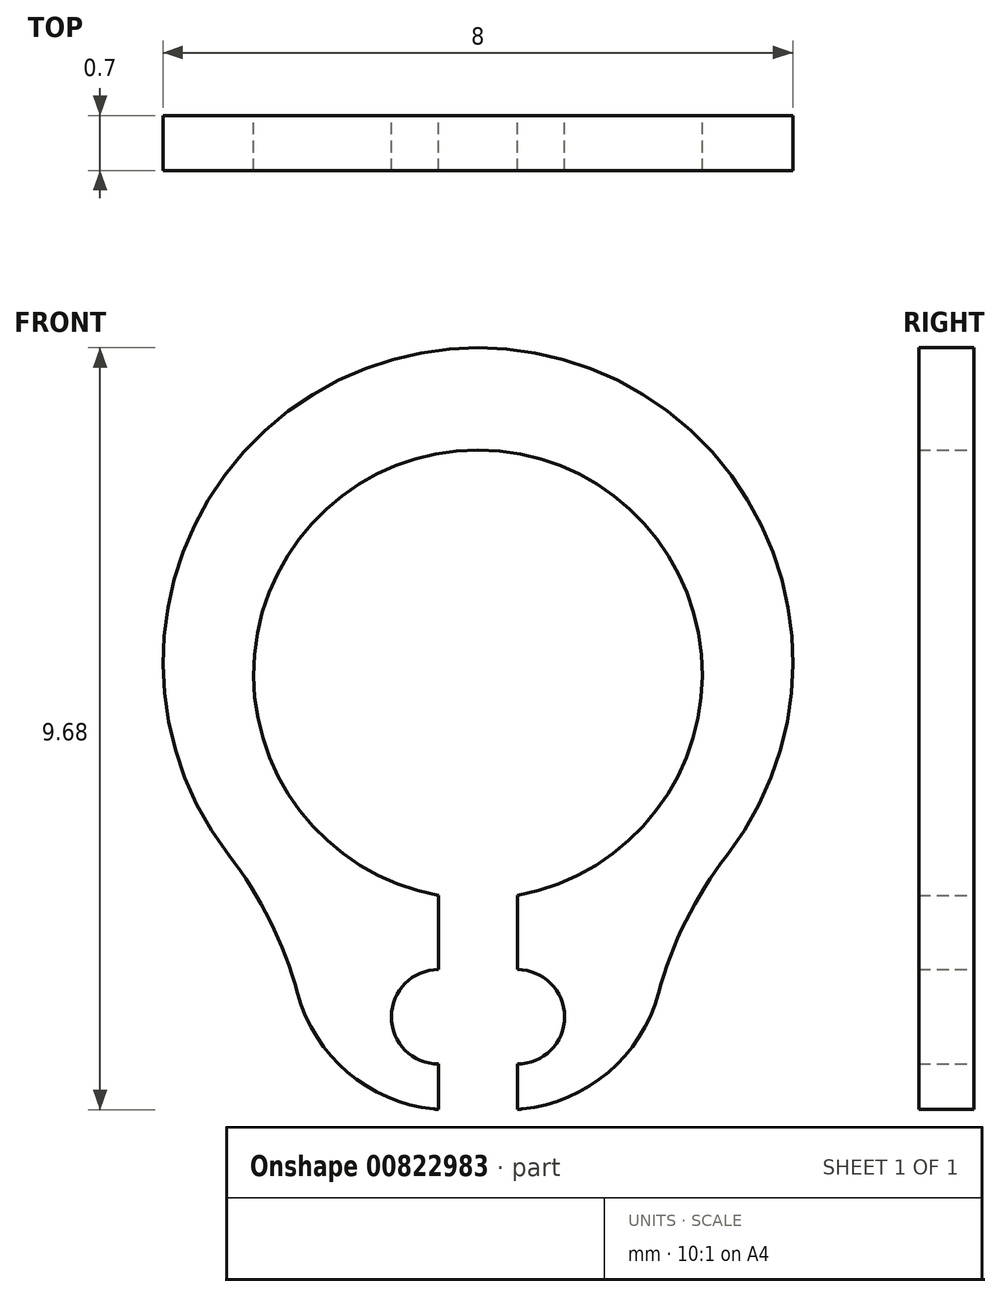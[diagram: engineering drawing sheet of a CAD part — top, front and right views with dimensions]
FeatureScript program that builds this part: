
annotation { "Feature Type Name" : "Feature", "Feature Type Description" : "" }
export const myFeature = defineFeature(function(context is Context, id is Id, definition is map)
    precondition{}
    {
        {
            var Q0;
            Q0=qCreatedBy(makeId("Front.planeOp"),FACE);
            var sketch = newSketch(context, id + "F0", { "sketchPlane" : qUnion([Q0])});
            skArc(sketch, "E0", {"start": v(0.5, -2.8) * mm, "mid": v(0, 2.85) * mm, "end": v(-0.5, -2.8) * mm});
            skLineSegment(sketch, "E1", {"start": v(0, 0) * mm, "end": v(0, -5.55) * mm, "construction": true});
            skLineSegment(sketch, "E2", {"start": v(0, 0) * mm, "end": v(0, 2.85) * mm, "construction": true});
            skLineSegment(sketch, "E3", {"start": v(0, 2.85) * mm, "end": v(0, 4.15) * mm, "construction": true});
            skPoint(sketch, "E4", {"position": v(0, -2.85) * mm});
            skArc(sketch, "E5", {"start": v(-2.12, -5.13) * mm, "mid": v(-1.33, -5.39) * mm, "end": v(-0.5, -5.53) * mm});
            skArc(sketch, "E6", {"start": v(1.48, -3.57) * mm, "mid": v(0, 4.15) * mm, "end": v(-1.48, -3.57) * mm});
            skPoint(sketch, "E7", {"position": v(0, -3.85) * mm});
            skArc(sketch, "E8", {"start": v(0.5, -4.95) * mm, "mid": v(1.1, -4.35) * mm, "end": v(0.5, -3.75) * mm});
            skLineSegment(sketch, "E9", {"start": v(0, 0) * mm, "end": v(0.5, -1.2) * mm, "construction": true});
            skLineSegment(sketch, "E10.0", {"start": v(-0.5, 0) * mm, "end": v(-0.5, -1.2) * mm, "construction": true});
            skLineSegment(sketch, "E11.MirrorCS", {"start": v(0.5, 0) * mm, "end": v(0.5, -1.2) * mm, "construction": true});
            skArc(sketch, "E12.MirrorC", {"start": v(-0.17, -3.85) * mm, "mid": v(0.09, -4.23) * mm, "end": v(0, -4.68) * mm, "construction": true});
            skLineSegment(sketch, "E13.MirrorCS", {"start": v(0, 0) * mm, "end": v(-0.5, -1.2) * mm, "construction": true});
            skLineSegment(sketch, "E14.trimOffspring", {"start": v(-0.5, -2.8) * mm, "end": v(-0.5, -3.75) * mm});
            skLineSegment(sketch, "E15.trimOffspring", {"start": v(0.5, -2.8) * mm, "end": v(0.5, -3.75) * mm});
            skLineSegment(sketch, "E16.trimOffspring", {"start": v(1.48, -3.57) * mm, "end": v(2.12, -5.13) * mm});
            skLineSegment(sketch, "E17.trimOffspring", {"start": v(-1.48, -3.57) * mm, "end": v(-2.12, -5.13) * mm});
            skPoint(sketch, "E18.orphan", {"position": v(-3.32, -8.02) * mm});
            skPoint(sketch, "E19.orphan", {"position": v(3.32, -8.02) * mm});
            skPoint(sketch, "E20.orphan", {"position": v(-0.5, -7.44) * mm});
            skPoint(sketch, "E21.orphan", {"position": v(0.5, -7.44) * mm});
            skArc(sketch, "E22.trimOffspring", {"start": v(-0.7, -3.79) * mm, "mid": v(0, -3.85) * mm, "end": v(0.7, -3.79) * mm, "construction": true});
            skLineSegment(sketch, "E23.trimOffspring", {"start": v(-0.5, -4.95) * mm, "end": v(-0.5, -5.53) * mm});
            skLineSegment(sketch, "E24.trimOffspring", {"start": v(-0.5, -3.82) * mm, "end": v(-0.5, -4.35) * mm, "construction": true});
            skLineSegment(sketch, "E25.trimOffspring", {"start": v(0.5, -3.82) * mm, "end": v(0.5, -4.35) * mm, "construction": true});
            skLineSegment(sketch, "E26.trimOffspring", {"start": v(0.5, -4.95) * mm, "end": v(0.5, -5.53) * mm});
            skArc(sketch, "E27.trimOffspring", {"start": v(-0.5, -4.95) * mm, "mid": v(-1.1, -4.35) * mm, "end": v(-0.5, -3.75) * mm});
            skArc(sketch, "E28.trimOffspring", {"start": v(0.17, -3.85) * mm, "mid": v(-0.09, -4.23) * mm, "end": v(0, -4.68) * mm, "construction": true});
            skArc(sketch, "E29.trimOffspring", {"start": v(0.5, -5.53) * mm, "mid": v(1.33, -5.39) * mm, "end": v(2.12, -5.13) * mm});
            skSolve(sketch);
        }
        {
            var Q0;
            Q0 = qSketchRegion(id + "F0", true);
            var Q1;
            Q1 = qConstructionFilter(qBodyType(qCreatedBy(id + "F0" ,EDGE), BodyType.WIRE), ConstructionObject.NO);
            extrude(context, id + "F1", {"entities" : qUnion([Q0]), "surfaceEntities" : qUnion([Q1]), "endBound" : BoundingType.SYMMETRIC, "depth" : 0.7 * mm, "offsetDistance" : 25 * mm});
        }
        {
            var Q0;
            Q0=makeQuery(id+"F1.opExtrude","SWEPT_EDGE",EDGE,{"disambiguationData":[OSD([sQuery(id+"F0.wireOp",EDGE,"E6"),sQuery(id+"F0.wireOp",EDGE,"E16.trimOffspring")])]});
            var Q1;
            Q1=makeQuery(id+"F1.opExtrude","SWEPT_EDGE",EDGE,{"disambiguationData":[OSD([sQuery(id+"F0.wireOp",EDGE,"E6"),sQuery(id+"F0.wireOp",EDGE,"E17.trimOffspring")])]});
            fillet(context, id + "F2", {"entities" : qUnion([Q0, Q1]), "radius" : 5 * mm, "tangentPropagation" : true, "allowEdgeOverflow" : false});
        }
        {
            var Q0;
            Q0=makeQuery(id+"F2.opFillet","BLEND_EDGE",EDGE,{"blendedFrom":[makeQuery(id+"F1.opExtrude","SWEPT_EDGE",EDGE,{"disambiguationData":[OSD([sQuery(id+"F0.wireOp",EDGE,"E6"),sQuery(id+"F0.wireOp",EDGE,"E17.trimOffspring")])]}),makeQuery(id+"F1.opExtrude","SWEPT_FACE",FACE,{"disambiguationData":[OSD([sQuery(id+"F0.wireOp",EDGE,"E5")])]})],"blendedInto":[makeQuery(id+"F1.opExtrude","SWEPT_FACE",FACE,{"disambiguationData":[OSD([sQuery(id+"F0.wireOp",EDGE,"E5")])]})]});
            var Q1;
            Q1=makeQuery(id+"F2.opFillet","BLEND_EDGE",EDGE,{"blendedFrom":[makeQuery(id+"F1.opExtrude","SWEPT_EDGE",EDGE,{"disambiguationData":[OSD([sQuery(id+"F0.wireOp",EDGE,"E6"),sQuery(id+"F0.wireOp",EDGE,"E16.trimOffspring")])]}),makeQuery(id+"F1.opExtrude","SWEPT_FACE",FACE,{"disambiguationData":[OSD([sQuery(id+"F0.wireOp",EDGE,"E29.trimOffspring")])]})],"blendedInto":[makeQuery(id+"F1.opExtrude","SWEPT_FACE",FACE,{"disambiguationData":[OSD([sQuery(id+"F0.wireOp",EDGE,"E29.trimOffspring")])]})]});
            fillet(context, id + "F3", {"entities" : qUnion([Q0, Q1]), "radius" : 2 * mm, "tangentPropagation" : true, "allowEdgeOverflow" : false});
        }
    });
